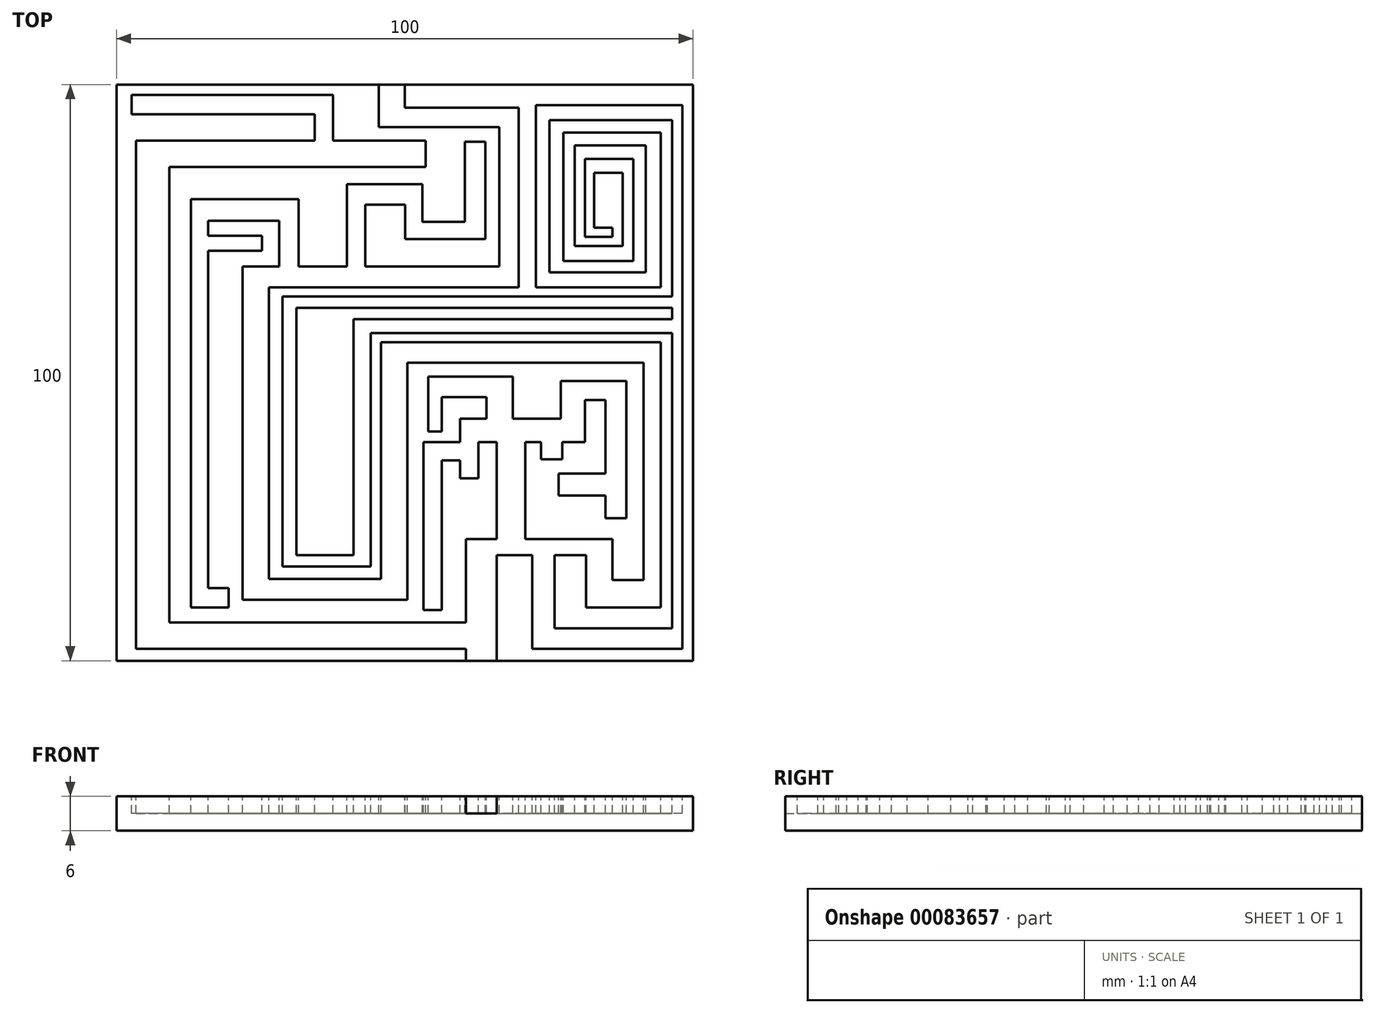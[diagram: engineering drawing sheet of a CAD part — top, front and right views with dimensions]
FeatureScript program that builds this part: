
annotation { "Feature Type Name" : "Feature", "Feature Type Description" : "" }
export const myFeature = defineFeature(function(context is Context, id is Id, definition is map)
    precondition{}
    {
        {
            var Q0;
            Q0=qCreatedBy(makeId("Top.planeOp"),FACE);
            var sketch = newSketch(context, id + "F0", { "sketchPlane" : qUnion([Q0])});
            skLineSegment(sketch, "E0.bottom", {"start": v(51.72, 62.07) * mm, "end": v(-48.28, 62.07) * mm});
            skLineSegment(sketch, "E0.top", {"start": v(51.72, -37.93) * mm, "end": v(-48.28, -37.93) * mm});
            skLineSegment(sketch, "E0.left", {"start": v(51.72, 62.07) * mm, "end": v(51.72, -37.93) * mm});
            skLineSegment(sketch, "E0.right", {"start": v(-48.28, 62.07) * mm, "end": v(-48.28, -37.93) * mm});
            skSolve(sketch);
        }
        {
            var Q0;
            Q0 = qSketchRegion(id + "F0", true);
            extrude(context, id + "F1", {"entities" : qUnion([Q0]), "depth" : 6 * mm});
        }
        {
            var Q0;
            Q0=makeQuery(id+"F1.opExtrude","CAP_FACE",FACE,{"disambiguationData":[OSD([sQuery(id+"F0.wireOp",EDGE,"E0.bottom"),sQuery(id+"F0.wireOp",EDGE,"E0.top"),sQuery(id+"F0.wireOp",EDGE,"E0.left"),sQuery(id+"F0.wireOp",EDGE,"E0.right")])],"isStart":false});
            var sketch = newSketch(context, id + "F2", { "sketchPlane" : qUnion([Q0])});
            skLineSegment(sketch, "E1.bottom", {"start": v(12.31, -37.93) * mm, "end": v(17.68, -37.93) * mm});
            skLineSegment(sketch, "E1.top", {"start": v(12.31, -16.78) * mm, "end": v(17.68, -16.78) * mm});
            skLineSegment(sketch, "E1.left", {"start": v(12.31, -37.93) * mm, "end": v(12.31, -35.85) * mm});
            skLineSegment(sketch, "E1.right", {"start": v(17.68, -37.93) * mm, "end": v(17.68, -19.56) * mm});
            skLineSegment(sketch, "E2.bottom", {"start": v(17.68, -16.78) * mm, "end": v(37.74, -16.78) * mm});
            skLineSegment(sketch, "E2.top", {"start": v(17.68, -19.56) * mm, "end": v(23.83, -19.56) * mm});
            skLineSegment(sketch, "E2.right", {"start": v(37.74, -16.78) * mm, "end": v(37.74, -19.56) * mm});
            skLineSegment(sketch, "E3.top", {"start": v(37.74, -28.7) * mm, "end": v(33.17, -28.7) * mm});
            skLineSegment(sketch, "E3.left", {"start": v(37.74, -19.56) * mm, "end": v(37.74, -23.93) * mm});
            skLineSegment(sketch, "E3.right", {"start": v(33.17, -19.56) * mm, "end": v(33.17, -28.7) * mm});
            skLineSegment(sketch, "E4.bottom", {"start": v(37.74, -28.7) * mm, "end": v(43.1, -28.7) * mm});
            skLineSegment(sketch, "E4.top", {"start": v(37.74, -23.93) * mm, "end": v(43.1, -23.93) * mm});
            skLineSegment(sketch, "E5.bottom", {"start": v(43.1, -28.7) * mm, "end": v(46.08, -28.7) * mm});
            skLineSegment(sketch, "E5.top", {"start": v(43.1, 17.38) * mm, "end": v(46.08, 17.38) * mm});
            skLineSegment(sketch, "E5.left", {"start": v(43.1, -23.93) * mm, "end": v(43.1, 13.8) * mm});
            skLineSegment(sketch, "E5.right", {"start": v(46.08, -28.7) * mm, "end": v(46.08, 17.38) * mm});
            skLineSegment(sketch, "E6.bottom", {"start": v(43.1, 17.38) * mm, "end": v(2.18, 17.38) * mm});
            skLineSegment(sketch, "E6.top", {"start": v(43.1, 13.8) * mm, "end": v(2.18, 13.8) * mm});
            skLineSegment(sketch, "E7.bottom", {"start": v(2.18, 17.38) * mm, "end": v(-2.38, 17.38) * mm});
            skLineSegment(sketch, "E7.top", {"start": v(2.18, -27.3) * mm, "end": v(-2.38, -27.3) * mm});
            skLineSegment(sketch, "E7.left", {"start": v(2.18, 13.8) * mm, "end": v(2.18, -27.3) * mm});
            skLineSegment(sketch, "E7.right", {"start": v(-2.38, 17.38) * mm, "end": v(-2.38, -23.73) * mm});
            skLineSegment(sketch, "E8.bottom", {"start": v(-2.38, -27.3) * mm, "end": v(-26.42, -27.3) * mm});
            skLineSegment(sketch, "E8.top", {"start": v(-2.38, -23.73) * mm, "end": v(-21.85, -23.73) * mm});
            skLineSegment(sketch, "E8.right", {"start": v(-26.42, -27.3) * mm, "end": v(-26.42, -23.73) * mm});
            skLineSegment(sketch, "E9.top", {"start": v(-26.42, 30.49) * mm, "end": v(-21.85, 30.49) * mm});
            skLineSegment(sketch, "E9.left", {"start": v(-26.42, -23.73) * mm, "end": v(-26.42, 30.49) * mm});
            skLineSegment(sketch, "E9.right", {"start": v(-21.85, -23.73) * mm, "end": v(-21.85, 26.91) * mm});
            skLineSegment(sketch, "E10.bottom", {"start": v(-21.85, 30.49) * mm, "end": v(-20.06, 30.49) * mm});
            skLineSegment(sketch, "E10.top", {"start": v(-21.85, 26.91) * mm, "end": v(18.07, 26.91) * mm});
            skLineSegment(sketch, "E11.bottom", {"start": v(18.07, 26.91) * mm, "end": v(21.45, 26.91) * mm});
            skLineSegment(sketch, "E11.top", {"start": v(18.07, 58.1) * mm, "end": v(21.45, 58.1) * mm});
            skLineSegment(sketch, "E11.left", {"start": v(18.07, 30.49) * mm, "end": v(18.07, 54.72) * mm});
            skLineSegment(sketch, "E11.right", {"start": v(21.45, 26.91) * mm, "end": v(21.45, 58.1) * mm});
            skLineSegment(sketch, "E12.bottom", {"start": v(18.07, 58.1) * mm, "end": v(1.72, 58.1) * mm});
            skLineSegment(sketch, "E12.top", {"start": v(18.07, 54.72) * mm, "end": v(-2.78, 54.72) * mm});
            skLineSegment(sketch, "E12.right", {"start": v(-2.78, 58.1) * mm, "end": v(-2.78, 54.72) * mm});
            skLineSegment(sketch, "E13.top", {"start": v(-2.78, 62.07) * mm, "end": v(1.72, 62.07) * mm});
            skLineSegment(sketch, "E13.left", {"start": v(-2.78, 58.1) * mm, "end": v(-2.78, 62.07) * mm});
            skLineSegment(sketch, "E13.right", {"start": v(1.72, 58.1) * mm, "end": v(1.72, 62.07) * mm});
            skLineSegment(sketch, "E14.left", {"start": v(17.68, -16.78) * mm, "end": v(17.68, 0) * mm});
            skLineSegment(sketch, "E14.right", {"start": v(22.64, -16.78) * mm, "end": v(22.64, 0) * mm});
            skLineSegment(sketch, "E15.bottom", {"start": v(22.64, 0) * mm, "end": v(25.32, 0) * mm});
            skLineSegment(sketch, "E15.top", {"start": v(20.46, 4.07) * mm, "end": v(28.8, 4.07) * mm});
            skLineSegment(sketch, "E15.right", {"start": v(32.97, 0) * mm, "end": v(32.97, 4.07) * mm});
            skLineSegment(sketch, "E16.top", {"start": v(32.97, 10.63) * mm, "end": v(28.8, 10.63) * mm});
            skLineSegment(sketch, "E16.left", {"start": v(32.97, 4.07) * mm, "end": v(32.97, 7.35) * mm});
            skLineSegment(sketch, "E16.right", {"start": v(28.8, 4.07) * mm, "end": v(28.8, 10.63) * mm});
            skPoint(sketch, "E17.oppositeSnap0", {"position": v(32.97, 7.35) * mm});
            skLineSegment(sketch, "E17.bottom", {"start": v(32.97, 10.63) * mm, "end": v(40.12, 10.63) * mm});
            skLineSegment(sketch, "E17.top", {"start": v(32.97, 7.35) * mm, "end": v(36.54, 7.35) * mm});
            skLineSegment(sketch, "E17.right", {"start": v(40.12, 10.63) * mm, "end": v(40.12, 7.35) * mm});
            skLineSegment(sketch, "E18.top", {"start": v(40.12, -13.2) * mm, "end": v(36.54, -13.2) * mm});
            skLineSegment(sketch, "E18.left", {"start": v(40.12, 7.35) * mm, "end": v(40.12, -13.2) * mm});
            skLineSegment(sketch, "E18.right", {"start": v(36.54, 7.35) * mm, "end": v(36.54, -5.46) * mm});
            skLineSegment(sketch, "E19.bottom", {"start": v(36.54, -5.46) * mm, "end": v(28.4, -5.46) * mm});
            skLineSegment(sketch, "E19.top", {"start": v(36.54, -9.24) * mm, "end": v(28.4, -9.24) * mm});
            skLineSegment(sketch, "E19.right", {"start": v(28.4, -5.46) * mm, "end": v(28.4, -9.24) * mm});
            skPoint(sketch, "E20.oppositeSnap0", {"position": v(25.32, 0) * mm});
            skPoint(sketch, "E20.oppositeSnap1", {"position": v(36.54, -2.93) * mm});
            skLineSegment(sketch, "E20.top", {"start": v(29, -2.93) * mm, "end": v(25.32, -2.93) * mm});
            skLineSegment(sketch, "E20.left", {"start": v(29, 0) * mm, "end": v(29, -2.93) * mm});
            skLineSegment(sketch, "E20.right", {"start": v(25.32, 0) * mm, "end": v(25.32, -2.93) * mm});
            skLineSegment(sketch, "E21.bottom", {"start": v(15.89, 4.07) * mm, "end": v(11.32, 4.07) * mm});
            skLineSegment(sketch, "E21.top", {"start": v(17.68, 0) * mm, "end": v(14.5, 0) * mm});
            skLineSegment(sketch, "E21.right", {"start": v(11.32, 4.07) * mm, "end": v(11.32, 0) * mm});
            skPoint(sketch, "E22.oppositeSnap0", {"position": v(14.5, 0) * mm});
            skLineSegment(sketch, "E22.top", {"start": v(11.32, -6.26) * mm, "end": v(14.5, -6.26) * mm});
            skLineSegment(sketch, "E22.left", {"start": v(11.32, -3.13) * mm, "end": v(11.32, -6.26) * mm});
            skLineSegment(sketch, "E22.right", {"start": v(14.5, 0) * mm, "end": v(14.5, -6.26) * mm});
            skPoint(sketch, "E23.oppositeSnap0", {"position": v(11.32, -3.13) * mm});
            skLineSegment(sketch, "E23.bottom", {"start": v(11.32, 0) * mm, "end": v(4.97, 0) * mm});
            skLineSegment(sketch, "E23.top", {"start": v(11.32, -3.13) * mm, "end": v(8.14, -3.13) * mm});
            skLineSegment(sketch, "E23.right", {"start": v(4.97, 0) * mm, "end": v(4.97, -3.13) * mm});
            skLineSegment(sketch, "E24.top", {"start": v(27.7, -35.85) * mm, "end": v(23.83, -35.85) * mm});
            skLineSegment(sketch, "E24.left", {"start": v(27.7, -19.56) * mm, "end": v(27.7, -32.27) * mm});
            skLineSegment(sketch, "E24.right", {"start": v(23.83, -19.56) * mm, "end": v(23.83, -35.85) * mm});
            skLineSegment(sketch, "E25.bottom", {"start": v(27.7, -35.85) * mm, "end": v(49.85, -35.85) * mm});
            skLineSegment(sketch, "E25.top", {"start": v(27.7, -32.27) * mm, "end": v(48.06, -32.27) * mm});
            skLineSegment(sketch, "E25.right", {"start": v(49.85, -35.85) * mm, "end": v(49.85, -32.27) * mm});
            skLineSegment(sketch, "E26.top", {"start": v(49.85, 58.5) * mm, "end": v(48.06, 58.5) * mm});
            skLineSegment(sketch, "E26.left", {"start": v(49.85, -32.27) * mm, "end": v(49.85, 58.5) * mm});
            skLineSegment(sketch, "E26.right", {"start": v(48.06, -32.27) * mm, "end": v(48.06, 18.97) * mm});
            skLineSegment(sketch, "E27.bottom", {"start": v(48.06, 58.5) * mm, "end": v(24.43, 58.5) * mm});
            skLineSegment(sketch, "E27.top", {"start": v(48.06, 55.9) * mm, "end": v(26.81, 55.9) * mm});
            skLineSegment(sketch, "E27.right", {"start": v(24.43, 58.5) * mm, "end": v(24.43, 55.9) * mm});
            skLineSegment(sketch, "E28.top", {"start": v(24.43, 26.91) * mm, "end": v(26.81, 26.91) * mm});
            skLineSegment(sketch, "E28.left", {"start": v(24.43, 55.9) * mm, "end": v(24.43, 26.91) * mm});
            skLineSegment(sketch, "E28.right", {"start": v(26.81, 55.9) * mm, "end": v(26.81, 29.5) * mm});
            skLineSegment(sketch, "E29.bottom", {"start": v(26.81, 26.91) * mm, "end": v(46.08, 26.91) * mm});
            skLineSegment(sketch, "E29.top", {"start": v(26.81, 29.5) * mm, "end": v(43.5, 29.5) * mm});
            skLineSegment(sketch, "E29.right", {"start": v(46.08, 26.91) * mm, "end": v(46.08, 29.5) * mm});
            skLineSegment(sketch, "E30.top", {"start": v(46.08, 53.72) * mm, "end": v(43.5, 53.72) * mm});
            skLineSegment(sketch, "E30.left", {"start": v(46.08, 29.5) * mm, "end": v(46.08, 53.72) * mm});
            skLineSegment(sketch, "E30.right", {"start": v(43.5, 29.5) * mm, "end": v(43.5, 51.54) * mm});
            skLineSegment(sketch, "E31.bottom", {"start": v(43.5, 53.72) * mm, "end": v(29.2, 53.72) * mm});
            skLineSegment(sketch, "E31.top", {"start": v(43.5, 51.54) * mm, "end": v(31.18, 51.54) * mm});
            skLineSegment(sketch, "E31.right", {"start": v(29.2, 53.72) * mm, "end": v(29.2, 51.54) * mm});
            skLineSegment(sketch, "E32.top", {"start": v(29.2, 31.48) * mm, "end": v(31.18, 31.48) * mm});
            skLineSegment(sketch, "E32.left", {"start": v(29.2, 51.54) * mm, "end": v(29.2, 31.48) * mm});
            skLineSegment(sketch, "E32.right", {"start": v(31.18, 51.54) * mm, "end": v(31.18, 34.06) * mm});
            skLineSegment(sketch, "E33.bottom", {"start": v(31.18, 31.48) * mm, "end": v(41.31, 31.48) * mm});
            skLineSegment(sketch, "E33.top", {"start": v(31.18, 34.06) * mm, "end": v(39.52, 34.06) * mm});
            skLineSegment(sketch, "E33.right", {"start": v(41.31, 31.48) * mm, "end": v(41.31, 34.06) * mm});
            skLineSegment(sketch, "E34.top", {"start": v(41.31, 49.16) * mm, "end": v(39.52, 49.16) * mm});
            skLineSegment(sketch, "E34.left", {"start": v(41.31, 34.06) * mm, "end": v(41.31, 49.16) * mm});
            skLineSegment(sketch, "E34.right", {"start": v(39.52, 34.06) * mm, "end": v(39.52, 46.77) * mm});
            skLineSegment(sketch, "E35.bottom", {"start": v(39.52, 49.16) * mm, "end": v(32.97, 49.16) * mm});
            skLineSegment(sketch, "E35.top", {"start": v(39.52, 46.77) * mm, "end": v(34.56, 46.77) * mm});
            skLineSegment(sketch, "E35.right", {"start": v(32.97, 49.16) * mm, "end": v(32.97, 46.77) * mm});
            skLineSegment(sketch, "E36.top", {"start": v(32.97, 35.65) * mm, "end": v(34.56, 35.65) * mm});
            skLineSegment(sketch, "E36.left", {"start": v(32.97, 46.77) * mm, "end": v(32.97, 35.65) * mm});
            skLineSegment(sketch, "E36.right", {"start": v(34.56, 46.77) * mm, "end": v(34.56, 37.24) * mm});
            skLineSegment(sketch, "E37.bottom", {"start": v(34.56, 35.65) * mm, "end": v(37.74, 35.65) * mm});
            skLineSegment(sketch, "E37.top", {"start": v(34.56, 37.24) * mm, "end": v(37.74, 37.24) * mm});
            skLineSegment(sketch, "E37.right", {"start": v(37.74, 35.65) * mm, "end": v(37.74, 37.24) * mm});
            skLineSegment(sketch, "E38.bottom", {"start": v(48.06, 18.97) * mm, "end": v(-4.17, 18.97) * mm});
            skLineSegment(sketch, "E38.top", {"start": v(48.06, 21.35) * mm, "end": v(-4.17, 21.35) * mm});
            skLineSegment(sketch, "E39.bottom", {"start": v(-4.17, 21.35) * mm, "end": v(-7.15, 21.35) * mm});
            skLineSegment(sketch, "E39.top", {"start": v(-4.17, -21.55) * mm, "end": v(-7.15, -21.55) * mm});
            skLineSegment(sketch, "E39.left", {"start": v(-4.17, 18.97) * mm, "end": v(-4.17, -21.55) * mm});
            skLineSegment(sketch, "E39.right", {"start": v(-7.15, 21.35) * mm, "end": v(-7.15, -19.56) * mm});
            skLineSegment(sketch, "E40.bottom", {"start": v(-7.15, -21.55) * mm, "end": v(-19.46, -21.55) * mm});
            skLineSegment(sketch, "E40.top", {"start": v(-7.15, -19.56) * mm, "end": v(-17.08, -19.56) * mm});
            skLineSegment(sketch, "E40.right", {"start": v(-19.46, -21.55) * mm, "end": v(-19.46, -19.56) * mm});
            skLineSegment(sketch, "E41.top", {"start": v(-19.46, 25.32) * mm, "end": v(-17.08, 25.32) * mm});
            skLineSegment(sketch, "E41.left", {"start": v(-19.46, -19.56) * mm, "end": v(-19.46, 25.32) * mm});
            skLineSegment(sketch, "E41.right", {"start": v(-17.08, -19.56) * mm, "end": v(-17.08, 23.34) * mm});
            skLineSegment(sketch, "E42.bottom", {"start": v(-17.08, 25.32) * mm, "end": v(48.06, 25.32) * mm});
            skLineSegment(sketch, "E42.top", {"start": v(-17.08, 23.34) * mm, "end": v(48.06, 23.34) * mm});
            skLineSegment(sketch, "E43.bottom", {"start": v(12.31, -35.85) * mm, "end": v(-44.89, -35.85) * mm});
            skLineSegment(sketch, "E43.top", {"start": v(12.31, -31.28) * mm, "end": v(-39.13, -31.28) * mm});
            skLineSegment(sketch, "E43.right", {"start": v(-44.89, -35.85) * mm, "end": v(-44.89, -31.28) * mm});
            skLineSegment(sketch, "E44.top", {"start": v(-44.89, 52.33) * mm, "end": v(-39.13, 52.33) * mm});
            skLineSegment(sketch, "E44.left", {"start": v(-44.89, -31.28) * mm, "end": v(-44.89, 52.33) * mm});
            skLineSegment(sketch, "E44.right", {"start": v(-39.13, -31.28) * mm, "end": v(-39.13, 47.77) * mm});
            skLineSegment(sketch, "E45.bottom", {"start": v(-39.13, 52.33) * mm, "end": v(5.36, 52.33) * mm});
            skLineSegment(sketch, "E45.top", {"start": v(-39.13, 47.77) * mm, "end": v(5.36, 47.77) * mm});
            skLineSegment(sketch, "E45.right", {"start": v(5.36, 52.33) * mm, "end": v(5.36, 47.77) * mm});
            skLineSegment(sketch, "E46.trimOffspring", {"start": v(12.31, -31.28) * mm, "end": v(12.31, -16.78) * mm});
            skLineSegment(sketch, "E47.trimOffspring", {"start": v(36.54, -9.24) * mm, "end": v(36.54, -13.2) * mm});
            skLineSegment(sketch, "E48.trimOffspring", {"start": v(29, 0) * mm, "end": v(32.97, 0) * mm});
            skLineSegment(sketch, "E49.trimOffspring", {"start": v(27.7, -19.56) * mm, "end": v(33.17, -19.56) * mm});
            skLineSegment(sketch, "E50.trimOffspring", {"start": v(48.06, 25.32) * mm, "end": v(48.06, 55.9) * mm});
            skLineSegment(sketch, "E51.trimOffspring", {"start": v(48.06, 21.35) * mm, "end": v(48.06, 23.34) * mm});
            skLineSegment(sketch, "E52.top", {"start": v(-20.06, 42.2) * mm, "end": v(-16.68, 42.2) * mm});
            skLineSegment(sketch, "E52.left", {"start": v(-20.06, 30.49) * mm, "end": v(-20.06, 38.43) * mm});
            skLineSegment(sketch, "E52.right", {"start": v(-16.68, 30.49) * mm, "end": v(-16.68, 42.2) * mm});
            skLineSegment(sketch, "E53.bottom", {"start": v(-20.06, 42.2) * mm, "end": v(-35.35, 42.2) * mm});
            skLineSegment(sketch, "E53.top", {"start": v(-20.06, 38.43) * mm, "end": v(-32.37, 38.43) * mm});
            skLineSegment(sketch, "E53.right", {"start": v(-35.35, 42.2) * mm, "end": v(-35.35, 38.43) * mm});
            skLineSegment(sketch, "E54.top", {"start": v(-35.35, -28.7) * mm, "end": v(-32.37, -28.7) * mm});
            skLineSegment(sketch, "E54.left", {"start": v(-35.35, 38.43) * mm, "end": v(-35.35, -28.7) * mm});
            skLineSegment(sketch, "E54.right", {"start": v(-32.37, 38.43) * mm, "end": v(-32.37, 35.85) * mm});
            skLineSegment(sketch, "E55.bottom", {"start": v(-32.37, 35.85) * mm, "end": v(-23.04, 35.85) * mm});
            skLineSegment(sketch, "E55.top", {"start": v(-32.37, 33.27) * mm, "end": v(-23.04, 33.27) * mm});
            skLineSegment(sketch, "E55.right", {"start": v(-23.04, 35.85) * mm, "end": v(-23.04, 33.27) * mm});
            skLineSegment(sketch, "E56.top", {"start": v(-8.34, 44.79) * mm, "end": v(-5.16, 44.79) * mm});
            skLineSegment(sketch, "E56.left", {"start": v(-8.34, 30.49) * mm, "end": v(-8.34, 44.79) * mm});
            skLineSegment(sketch, "E56.right", {"start": v(-5.16, 30.49) * mm, "end": v(-5.16, 41.21) * mm});
            skLineSegment(sketch, "E57.bottom", {"start": v(-5.16, 44.79) * mm, "end": v(4.77, 44.79) * mm});
            skLineSegment(sketch, "E57.top", {"start": v(-5.16, 41.21) * mm, "end": v(1.79, 41.21) * mm});
            skLineSegment(sketch, "E57.right", {"start": v(4.77, 44.79) * mm, "end": v(4.77, 41.21) * mm});
            skLineSegment(sketch, "E58.top", {"start": v(4.77, 35.25) * mm, "end": v(1.79, 35.25) * mm});
            skLineSegment(sketch, "E58.left", {"start": v(4.77, 41.21) * mm, "end": v(4.77, 38.23) * mm});
            skLineSegment(sketch, "E58.right", {"start": v(1.79, 41.21) * mm, "end": v(1.79, 35.25) * mm});
            skPoint(sketch, "E59.oppositeSnap0", {"position": v(4.77, 38.23) * mm});
            skLineSegment(sketch, "E59.bottom", {"start": v(4.77, 35.25) * mm, "end": v(15.7, 35.25) * mm});
            skLineSegment(sketch, "E59.top", {"start": v(4.77, 38.23) * mm, "end": v(12.12, 38.23) * mm});
            skLineSegment(sketch, "E59.right", {"start": v(15.7, 35.25) * mm, "end": v(15.7, 38.23) * mm});
            skLineSegment(sketch, "E60.top", {"start": v(15.7, 52.14) * mm, "end": v(12.12, 52.14) * mm});
            skLineSegment(sketch, "E60.left", {"start": v(15.7, 38.23) * mm, "end": v(15.7, 52.14) * mm});
            skLineSegment(sketch, "E60.right", {"start": v(12.12, 38.23) * mm, "end": v(12.12, 52.14) * mm});
            skLineSegment(sketch, "E61.trimOffspring", {"start": v(-16.68, 30.49) * mm, "end": v(-8.34, 30.49) * mm});
            skLineSegment(sketch, "E62.trimOffspring", {"start": v(-5.16, 30.49) * mm, "end": v(18.07, 30.49) * mm});
            skLineSegment(sketch, "E63.trimOffspring", {"start": v(-32.37, 33.27) * mm, "end": v(-32.37, -25.32) * mm});
            skLineSegment(sketch, "E64.top", {"start": v(4.97, -29.1) * mm, "end": v(8.14, -29.1) * mm});
            skLineSegment(sketch, "E64.left", {"start": v(4.97, -3.13) * mm, "end": v(4.97, -29.1) * mm});
            skLineSegment(sketch, "E64.right", {"start": v(8.14, -3.13) * mm, "end": v(8.14, -29.1) * mm});
            skLineSegment(sketch, "E65.bottom", {"start": v(-32.37, -28.7) * mm, "end": v(-28.8, -28.7) * mm});
            skLineSegment(sketch, "E65.top", {"start": v(-32.37, -25.32) * mm, "end": v(-28.8, -25.32) * mm});
            skLineSegment(sketch, "E65.right", {"start": v(-28.8, -28.7) * mm, "end": v(-28.8, -25.32) * mm});
            skLineSegment(sketch, "E66.top", {"start": v(20.46, 11.42) * mm, "end": v(15.89, 11.42) * mm});
            skLineSegment(sketch, "E66.left", {"start": v(20.46, 4.07) * mm, "end": v(20.46, 11.42) * mm});
            skLineSegment(sketch, "E66.right", {"start": v(15.89, 4.07) * mm, "end": v(15.89, 7.85) * mm});
            skLineSegment(sketch, "E67.bottom", {"start": v(15.89, 11.42) * mm, "end": v(5.76, 11.42) * mm});
            skLineSegment(sketch, "E67.top", {"start": v(15.89, 7.85) * mm, "end": v(8.14, 7.85) * mm});
            skLineSegment(sketch, "E67.right", {"start": v(5.76, 11.42) * mm, "end": v(5.76, 7.85) * mm});
            skPoint(sketch, "E68.oppositeSnap0", {"position": v(8.14, 0) * mm});
            skLineSegment(sketch, "E68.top", {"start": v(5.76, 1.89) * mm, "end": v(8.14, 1.89) * mm});
            skLineSegment(sketch, "E68.left", {"start": v(5.76, 7.85) * mm, "end": v(5.76, 1.89) * mm});
            skLineSegment(sketch, "E68.right", {"start": v(8.14, 7.85) * mm, "end": v(8.14, 1.89) * mm});
            skLineSegment(sketch, "E69.bottom", {"start": v(-10.73, 52.33) * mm, "end": v(-13.9, 52.33) * mm});
            skLineSegment(sketch, "E69.top", {"start": v(-10.73, 60.28) * mm, "end": v(-13.9, 60.28) * mm});
            skLineSegment(sketch, "E69.left", {"start": v(-10.73, 52.33) * mm, "end": v(-10.73, 60.28) * mm});
            skLineSegment(sketch, "E69.right", {"start": v(-13.9, 52.33) * mm, "end": v(-13.9, 60.28) * mm});
            skLineSegment(sketch, "E70.bottom", {"start": v(-13.9, 60.28) * mm, "end": v(-45.68, 60.28) * mm});
            skLineSegment(sketch, "E70.top", {"start": v(-13.9, 56.9) * mm, "end": v(-45.68, 56.9) * mm});
            skLineSegment(sketch, "E70.right", {"start": v(-45.68, 60.28) * mm, "end": v(-45.68, 56.9) * mm});
            skSolve(sketch);
        }
        {
            var Q0;
            Q0 = qSketchRegion(id + "F2", true);
            extrude(context, id + "F3", {"entities" : qUnion([Q0]), "operationType" : NewBodyOperationType.REMOVE, "oppositeDirection" : true, "depth" : 3 * mm});
        }
    });
